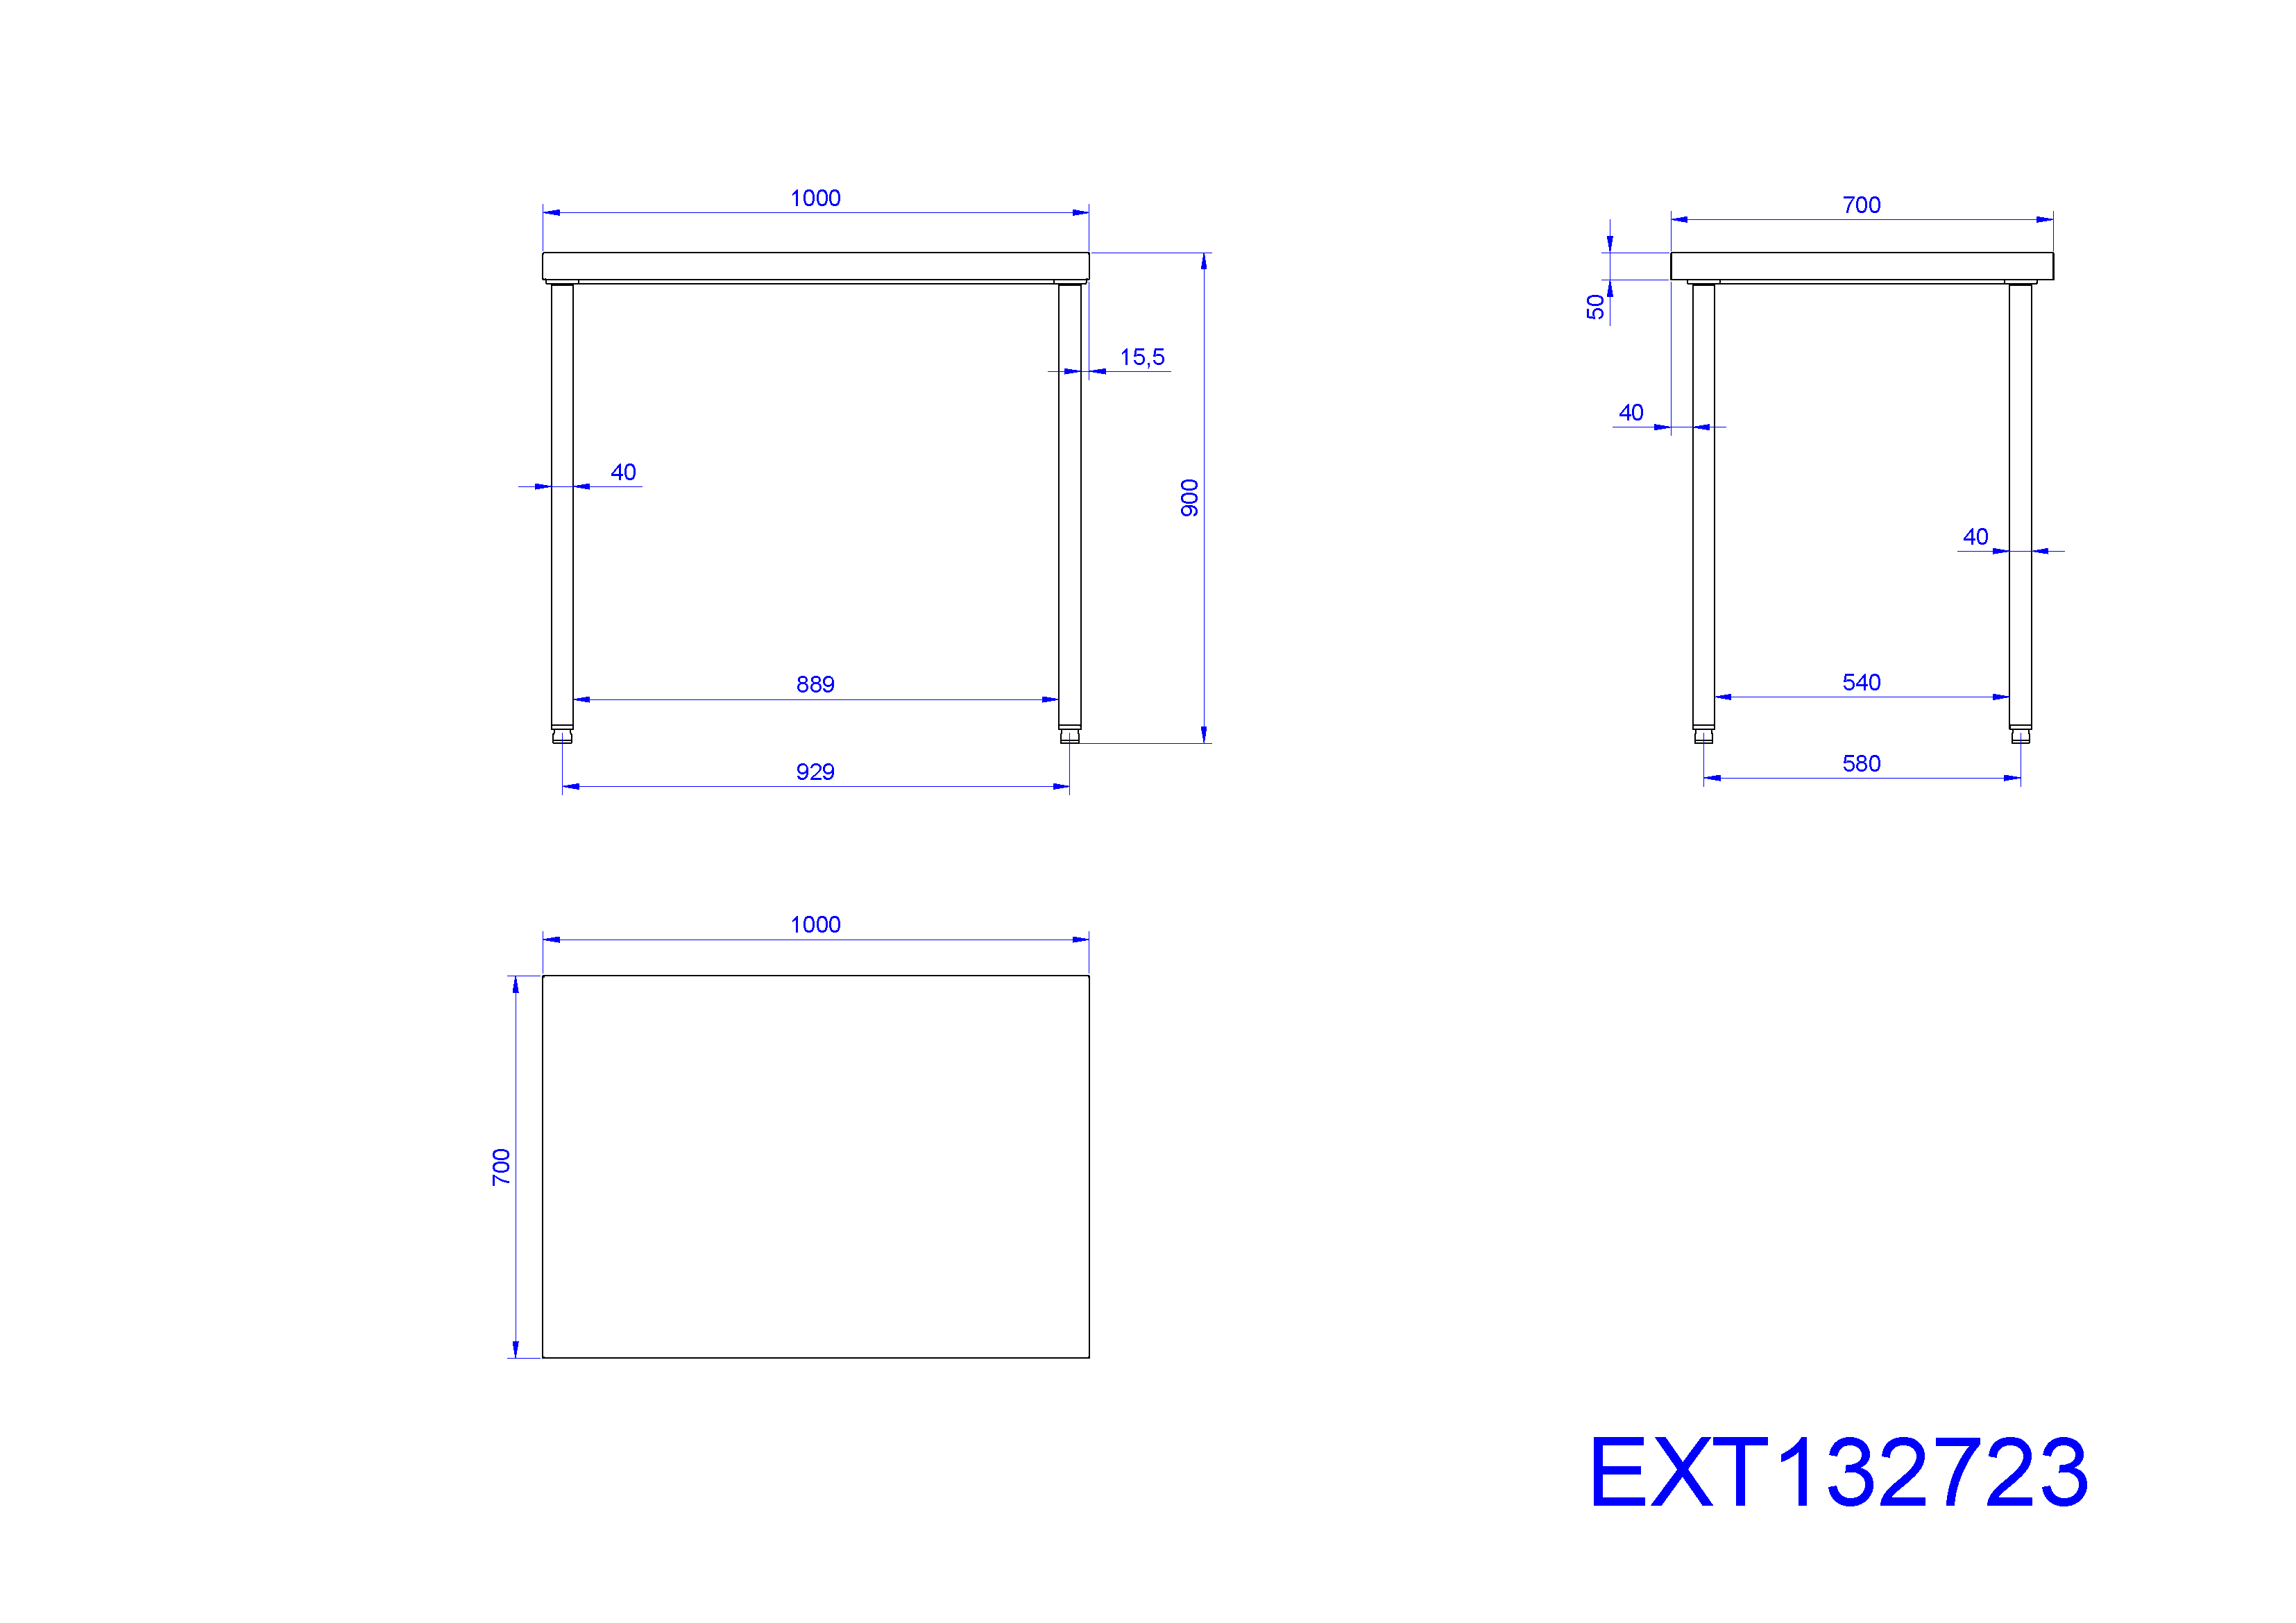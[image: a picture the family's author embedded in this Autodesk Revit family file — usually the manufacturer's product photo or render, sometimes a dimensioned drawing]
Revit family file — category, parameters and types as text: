
# Revit family: QF_ELECTROLUXPROFESSIONAL_133253_MLA2026SXPN
name_source: partatom
category: Attrezzature speciali
units: mm (PartAtom-declared; Revit-internal decimal feet)

## family parameters
Basato su piano di lavoro = No
Condiviso = No
Punto di calcolo locali = No
Quota connettore circolare = Usa diametro
Sempre verticale = Sì
Taglio con vuoti quando caricato = No
Tipo di parte = Normale

## types (1)
- Standard
    Accessory = Sì
    Cold Water Size = 0 mm
    Compressed Air Pressure = 0.0 Pa
    Compressed Air Size = 0 mm
    Compressed Air Volume = 0.0 L/s
    Condensate Return Size = 0 mm
    Cycle = 0 Hz
    Depth Actual = 700 mm  [stored 2.29659 ft]
    Descrizione = CUPB.SINK 2 BOWLS 600X500+L/H DRAIN.2000
    Direct Waste Size = 51 mm
    Gas Input Pressure = 0
    Gas KW = 0
    Gas Size = 0 mm
    HP = 0 HP
    Height Actual = 1000 mm  [stored 3.28084 ft]
    Hot Water Size = 0 mm
    Item Number = 133253
    Length Actual = 2000 mm  [stored 6.56168 ft]
    Modello = MLA2026SXPN
    Phase = 0
    Produttore = Electrolux Professional
    Prospetto di default = 0 mm  [stored 0 ft]
    Refrigerant Compressor Remote = Sì
    Refrigeration Liquid Line Size = 0 mm  [stored 0 ft]
    Refrigeration Suction Line Size = 0 mm  [stored 0 ft]
    Steam Consumption per Hour = 0
    Steam Supply Maximum Pressure = 0.0 Pa
    Steam Supply Minimum Pressure = 0.0 Pa
    Steam Supply Size = 0 mm
    URL = https://www.electroluxprofessional.com
    URL Manufacturer = https://www.electroluxprofessional.com
    Volts = 0 V
    Watts = 0 W
    Weight = 75.00 kg

note: source unit labels omitted for Gas Input Pressure — the stored unit's dimension contradicts the parameter name (converter mislabeling)

note: [stored X ft] marks values corroborated as IEEE doubles in the binary element streams (Revit-internal decimal feet)

## geometry (parser evidence)
native form markers: Blend x4, Sweep x2
no freeform markers — native parametric forms only
